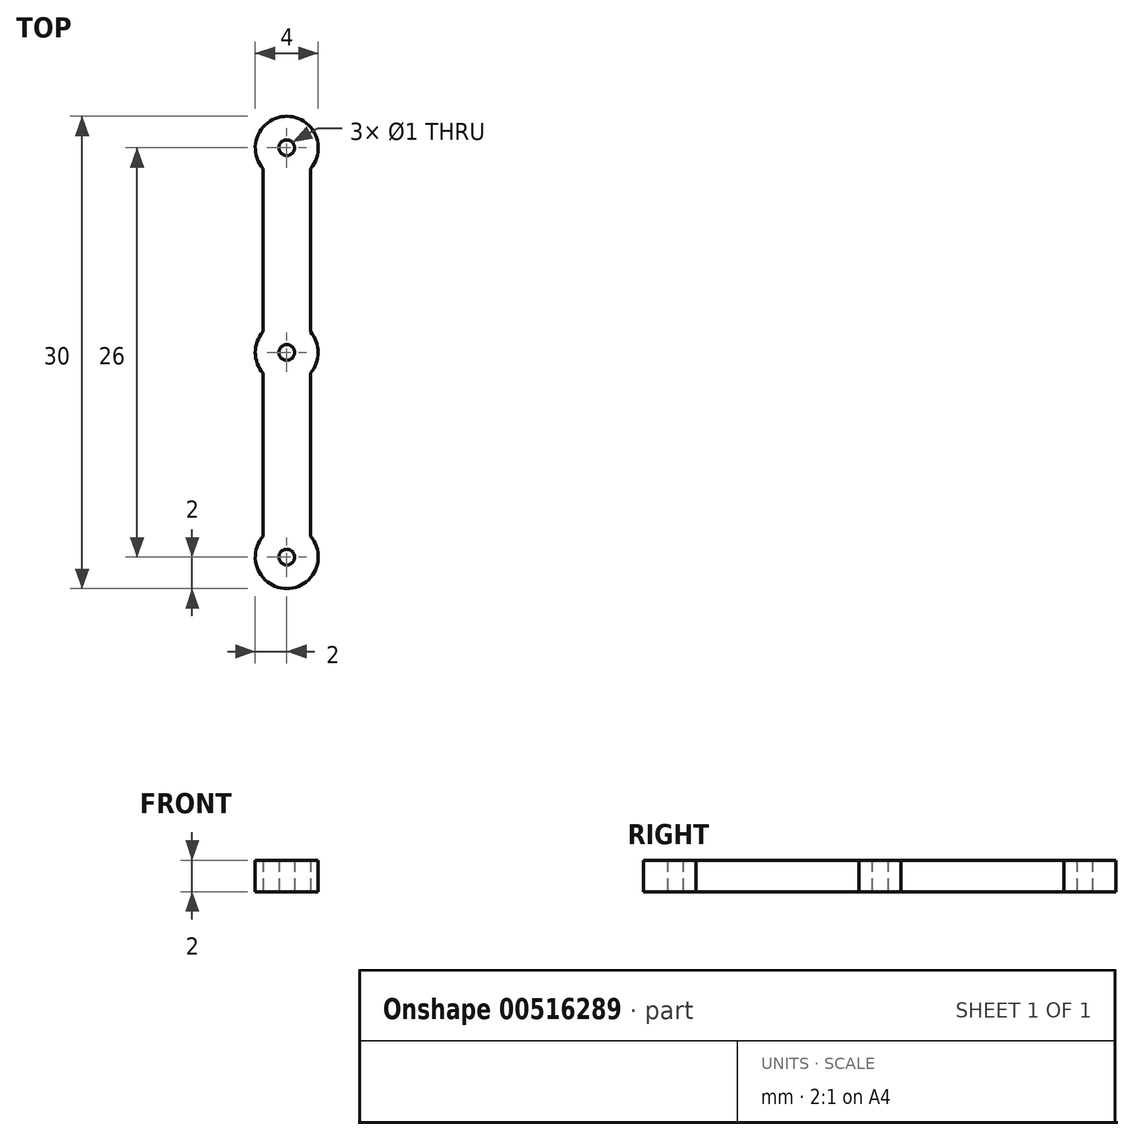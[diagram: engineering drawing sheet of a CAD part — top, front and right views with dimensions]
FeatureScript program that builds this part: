
annotation { "Feature Type Name" : "Feature", "Feature Type Description" : "" }
export const myFeature = defineFeature(function(context is Context, id is Id, definition is map)
    precondition{}
    {
        {
            var Q0;
            Q0=qCreatedBy(makeId("Top.planeOp"),FACE);
            var sketch = newSketch(context, id + "F0", { "sketchPlane" : qUnion([Q0])});
            skLineSegment(sketch, "E0.left", {"start": v(-1.5, 11.68) * mm, "end": v(-1.5, 1.32) * mm});
            skLineSegment(sketch, "E0.right", {"start": v(1.5, 11.68) * mm, "end": v(1.5, 1.32) * mm});
            skPoint(sketch, "E1", {"position": v(0, 13) * mm});
            skArc(sketch, "E2", {"start": v(1.5, 11.68) * mm, "mid": v(0, 15) * mm, "end": v(-1.5, 11.68) * mm});
            skPoint(sketch, "E3", {"position": v(0, -13) * mm});
            skArc(sketch, "E4", {"start": v(-1.5, -11.68) * mm, "mid": v(0, -15) * mm, "end": v(1.5, -11.68) * mm});
            skArc(sketch, "E5", {"start": v(-1.5, 1.32) * mm, "mid": v(-2, 0) * mm, "end": v(-1.5, -1.32) * mm});
            skLineSegment(sketch, "E6.trimOffspring", {"start": v(-1.5, -1.32) * mm, "end": v(-1.5, -11.68) * mm});
            skLineSegment(sketch, "E7.trimOffspring", {"start": v(1.5, -1.32) * mm, "end": v(1.5, -11.68) * mm});
            skArc(sketch, "E8.trimOffspring", {"start": v(1.5, -1.32) * mm, "mid": v(2, 0) * mm, "end": v(1.5, 1.32) * mm});
            skCircle(sketch, "E9", {"center": v(0, 13) * mm, "radius": 0.5 * mm});
            skCircle(sketch, "E10", {"center": v(0, 0) * mm, "radius": 0.5 * mm});
            skCircle(sketch, "E11", {"center": v(0, -13) * mm, "radius": 0.5 * mm});
            skSolve(sketch);
        }
        {
            var Q0;
            Q0 = qSketchRegion(id + "F0", true);
            extrude(context, id + "F1", {"entities" : qUnion([Q0]), "depth" : 2 * mm, "offsetDistance" : 25 * mm});
        }
    });
